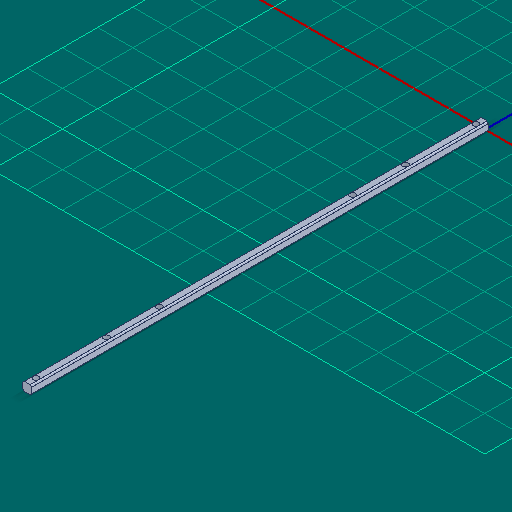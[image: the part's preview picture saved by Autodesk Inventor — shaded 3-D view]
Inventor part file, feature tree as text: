
AUTODESK INVENTOR PART (.ipt)
format: ipt  version: 2025 (Build 290162000, 162)  size: 199,168 bytes
history: native  units: in
note: dims shown in document units (in); Inventor stores cm internally (conversion verified against a paired STEP export)
features: extrude x3, sketch x3, thicken_offset x1, other x1
ambient origin geometry x8: Origin, YZ Plane, XZ Plane, XY Plane, X Axis, Y Axis, Z Axis, Center Point
bodies: Solid1 (feature_tree)
feature tree (8):
  extrude  "Extrusion1"  Depth=12.1875in
  thicken_offset  "Thicken1"
  extrude  "Extrusion2"  Depth=11.125in
  extrude  "Extrusion3"  Depth=0.165in
  sketch  "Sketch2"  dims[d0=0.0625in d1=0.0in d2=12.1875in]
  sketch  "Sketch3"  dims[d3=12.125in d4=11.125in]
  sketch  "Sketch4"  dims[d5=0.0in d6=0.165in d7=0.165in d8=1.0in d9=0.0in d10=0.165in d11=0.165in d12=0.165in d13=0.165in]
  other  "Cut-Revolve3"
